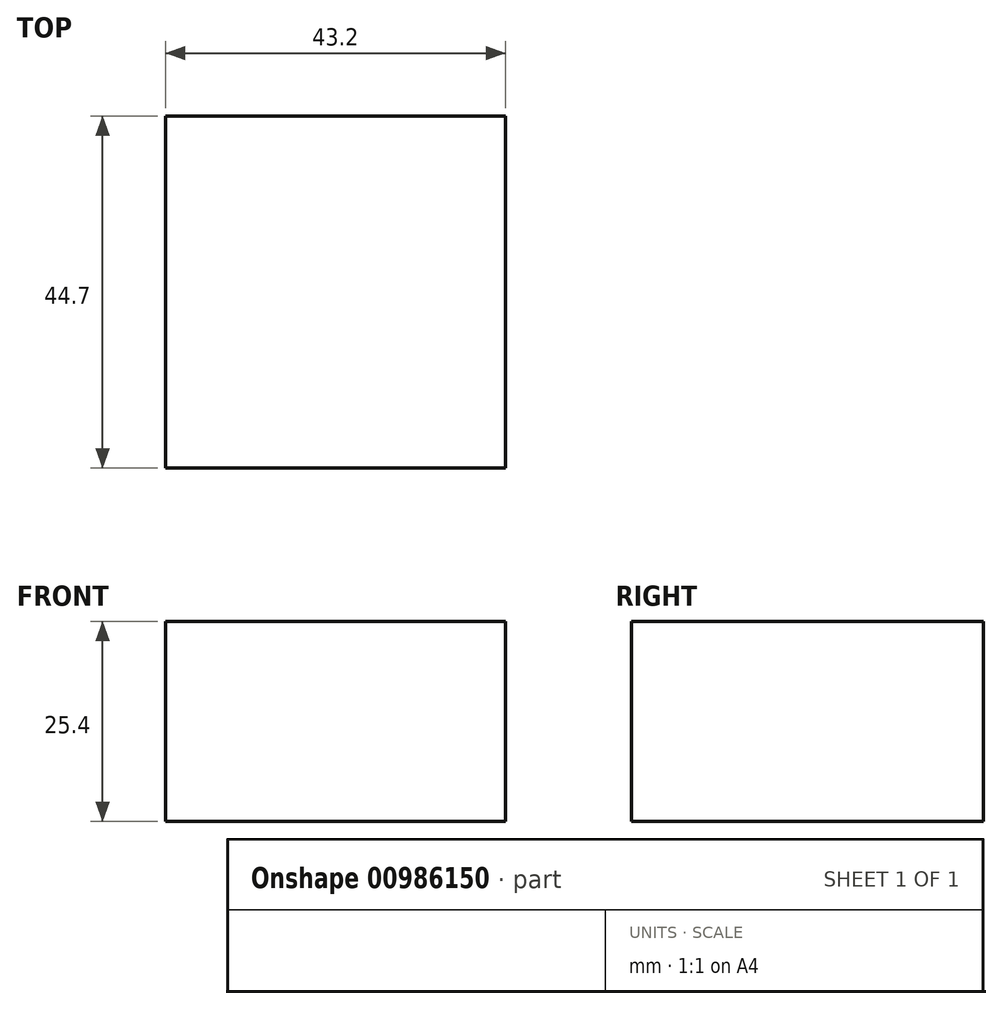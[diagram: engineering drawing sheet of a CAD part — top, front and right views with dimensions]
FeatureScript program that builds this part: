
annotation { "Feature Type Name" : "Feature", "Feature Type Description" : "" }
export const myFeature = defineFeature(function(context is Context, id is Id, definition is map)
    precondition{}
    {
        {
            var Q0;
            Q0=qCreatedBy(makeId("Top.planeOp"),FACE);
            var sketch = newSketch(context, id + "F0", { "sketchPlane" : qUnion([Q0])});
            skLineSegment(sketch, "E0.bottom", {"start": v(-15.3, 21) * mm, "end": v(27.9, 21) * mm});
            skLineSegment(sketch, "E0.top", {"start": v(-15.3, -23.7) * mm, "end": v(27.9, -23.7) * mm});
            skLineSegment(sketch, "E0.left", {"start": v(-15.3, 21) * mm, "end": v(-15.3, -23.7) * mm});
            skLineSegment(sketch, "E0.right", {"start": v(27.9, 21) * mm, "end": v(27.9, -23.7) * mm});
            skSolve(sketch);
        }
        {
            var Q0;
            Q0 = qSketchRegion(id + "F0", true);
            extrude(context, id + "F1", {"entities" : qUnion([Q0]), "depth" : 25.4 * mm, "offsetDistance" : 25.4 * mm});
        }
    });
